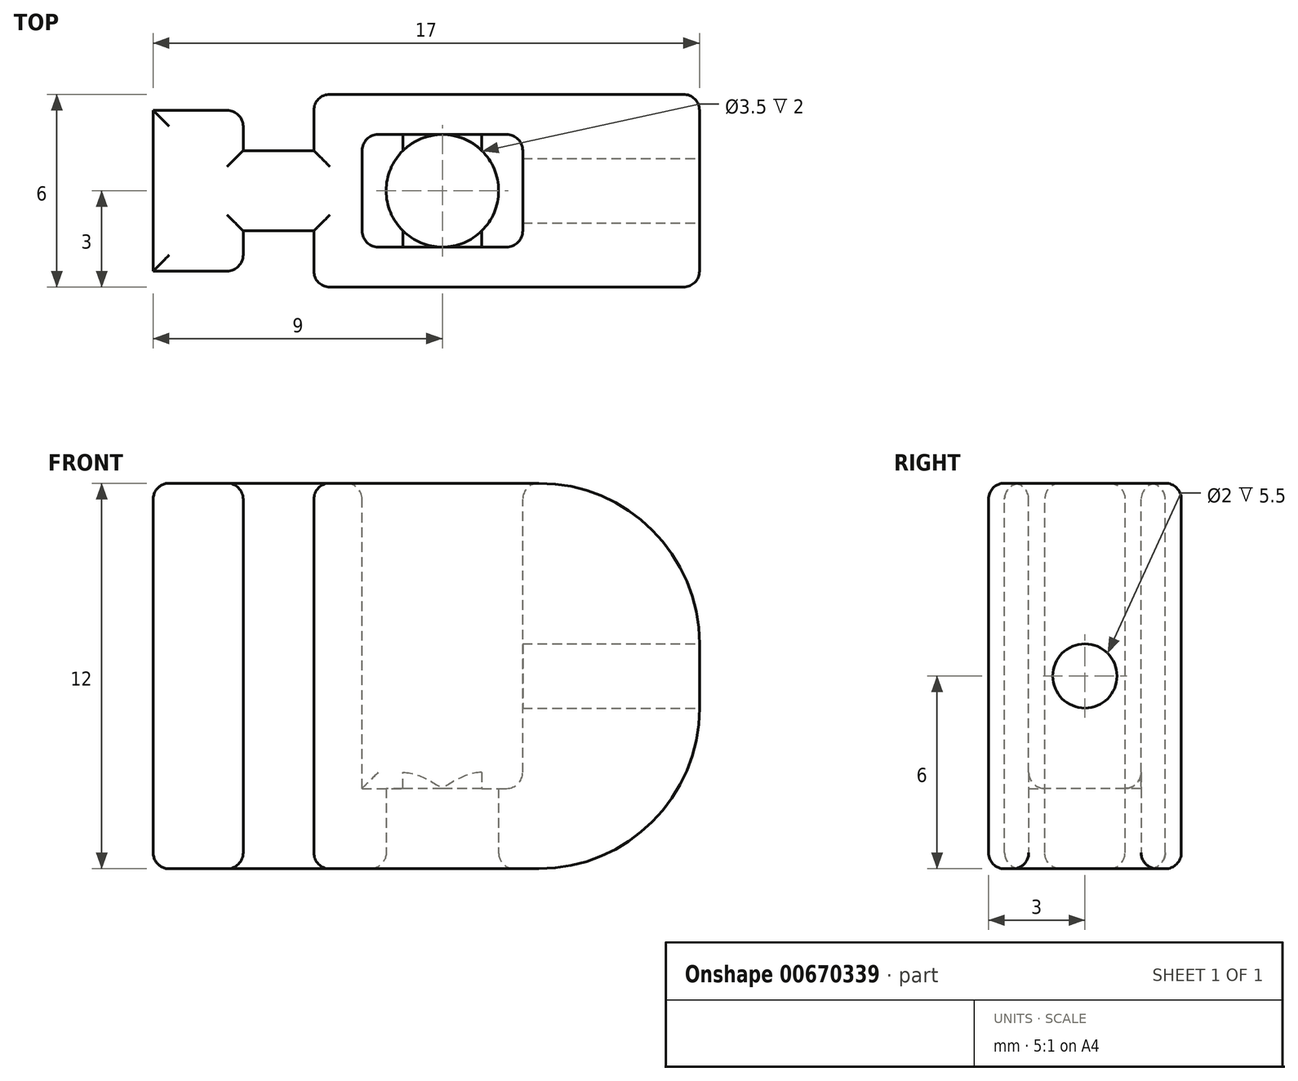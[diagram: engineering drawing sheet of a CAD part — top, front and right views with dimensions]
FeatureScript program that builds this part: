
annotation { "Feature Type Name" : "Feature", "Feature Type Description" : "" }
export const myFeature = defineFeature(function(context is Context, id is Id, definition is map)
    precondition{}
    {
        {
            var Q0;
            Q0=qCreatedBy(makeId("Top.planeOp"),FACE);
            var sketch = newSketch(context, id + "F0", { "sketchPlane" : qUnion([Q0])});
            skLineSegment(sketch, "E0.bottom", {"start": v(0, 0) * mm, "end": v(-17, 0) * mm});
            skLineSegment(sketch, "E0.top", {"start": v(0, 6) * mm, "end": v(-17, 6) * mm});
            skLineSegment(sketch, "E0.left", {"start": v(0, 0) * mm, "end": v(0, 6) * mm});
            skLineSegment(sketch, "E0.right", {"start": v(-17, 0) * mm, "end": v(-17, 6) * mm});
            skSolve(sketch);
        }
        {
            var Q0;
            Q0 = qSketchRegion(id + "F0", true);
            extrude(context, id + "F1", {"entities" : qUnion([Q0]), "depth" : 12 * mm, "offsetDistance" : 25 * mm});
        }
        {
            var Q0;
            Q0=makeQuery(id+"F1.opExtrude","CAP_FACE",FACE,{"disambiguationData":[OSD([sQuery(id+"F0.wireOp",EDGE,"E0.bottom"),sQuery(id+"F0.wireOp",EDGE,"E0.top"),sQuery(id+"F0.wireOp",EDGE,"E0.left"),sQuery(id+"F0.wireOp",EDGE,"E0.right")])],"isStart":false});
            var sketch = newSketch(context, id + "F2", { "sketchPlane" : qUnion([Q0])});
            skLineSegment(sketch, "E1", {"start": v(-17, 0) * mm, "end": v(-12, 0) * mm});
            skLineSegment(sketch, "E2", {"start": v(-12, 0) * mm, "end": v(-12, 1.75) * mm});
            skLineSegment(sketch, "E3", {"start": v(-12, 1.75) * mm, "end": v(-14.2, 1.75) * mm});
            skLineSegment(sketch, "E4", {"start": v(-14.2, 1.75) * mm, "end": v(-14.2, 0.5) * mm});
            skLineSegment(sketch, "E5", {"start": v(-14.2, 0.5) * mm, "end": v(-16.1, 0.5) * mm});
            skLineSegment(sketch, "E6", {"start": v(-16.1, 0.5) * mm, "end": v(-17, 0.5) * mm});
            skLineSegment(sketch, "E7", {"start": v(-17, 0.5) * mm, "end": v(-17, 5.5) * mm});
            skLineSegment(sketch, "E8", {"start": v(-17, 5.5) * mm, "end": v(-14.2, 5.5) * mm});
            skLineSegment(sketch, "E9", {"start": v(-14.2, 5.5) * mm, "end": v(-14.2, 4.25) * mm});
            skLineSegment(sketch, "E10", {"start": v(-14.2, 4.25) * mm, "end": v(-12, 4.25) * mm});
            skLineSegment(sketch, "E11", {"start": v(-12, 4.25) * mm, "end": v(-12, 6) * mm});
            skLineSegment(sketch, "E12", {"start": v(-12, 6) * mm, "end": v(-17.93, 6) * mm});
            skLineSegment(sketch, "E13", {"start": v(-17.93, 6) * mm, "end": v(-17.93, 0) * mm});
            skLineSegment(sketch, "E14", {"start": v(-17.93, 0) * mm, "end": v(-17, 0) * mm});
            skLineSegment(sketch, "E15", {"start": v(-21.87, 3) * mm, "end": v(11.12, 3) * mm, "construction": true});
            skSolve(sketch);
        }
        {
            var Q0;
            Q0 = qSketchRegion(id + "F2", true);
            extrude(context, id + "F3", {"entities" : qUnion([Q0]), "operationType" : NewBodyOperationType.REMOVE, "endBound" : BoundingType.THROUGH_ALL, "oppositeDirection" : true, "depth" : 25 * mm, "offsetDistance" : 25 * mm});
        }
        {
            var Q0;
            Q0=qCreatedBy(makeId("Top.planeOp"),FACE);
            var sketch = newSketch(context, id + "F4", { "sketchPlane" : qUnion([Q0])});
            skCircle(sketch, "E16", {"center": v(-8, 3) * mm, "radius": 1.75 * mm});
            skLineSegment(sketch, "E17", {"start": v(-20.02, 3) * mm, "end": v(4.02, 3) * mm, "construction": true});
            skSolve(sketch);
        }
        {
            var Q0;
            Q0 = qSketchRegion(id + "F4", true);
            extrude(context, id + "F5", {"entities" : qUnion([Q0]), "operationType" : NewBodyOperationType.REMOVE, "endBound" : BoundingType.THROUGH_ALL, "depth" : 25 * mm, "offsetDistance" : 25 * mm});
        }
        {
            var Q0;
            Q0=makeQuery(id+"F1.opExtrude","CAP_FACE",FACE,{"disambiguationData":[OSD([sQuery(id+"F0.wireOp",EDGE,"E0.bottom"),sQuery(id+"F0.wireOp",EDGE,"E0.top"),sQuery(id+"F0.wireOp",EDGE,"E0.left"),sQuery(id+"F0.wireOp",EDGE,"E0.right")])],"isStart":false});
            var sketch = newSketch(context, id + "F6", { "sketchPlane" : qUnion([Q0])});
            skLineSegment(sketch, "E18.bottom", {"start": v(-10.5, 4.75) * mm, "end": v(-5.5, 4.75) * mm});
            skLineSegment(sketch, "E18.top", {"start": v(-10.5, 1.25) * mm, "end": v(-5.5, 1.25) * mm});
            skLineSegment(sketch, "E18.left", {"start": v(-10.5, 4.75) * mm, "end": v(-10.5, 1.25) * mm});
            skLineSegment(sketch, "E18.right", {"start": v(-5.5, 4.75) * mm, "end": v(-5.5, 1.25) * mm});
            skLineSegment(sketch, "E19", {"start": v(-16.18, 3) * mm, "end": v(3.84, 3) * mm, "construction": true});
            skSolve(sketch);
        }
        {
            var Q0;
            Q0 = qSketchRegion(id + "F6", true);
            extrude(context, id + "F7", {"entities" : qUnion([Q0]), "operationType" : NewBodyOperationType.REMOVE, "oppositeDirection" : true, "depth" : 9.5 * mm, "offsetDistance" : 25 * mm});
        }
        {
            var Q0;
            Q0=makeQuery(id+"F3.boolean.opBoolean","COPY",EDGE,{"derivedFrom":makeQuery(id+"F3.opExtrude","SWEPT_EDGE",EDGE,{"disambiguationData":[OSD([sQuery(id+"F0.wireOp",EDGE,"E0.bottom"),sQuery(id+"F2.wireOp",EDGE,"E1"),sQuery(id+"F2.wireOp",EDGE,"E2")])]})});
            var Q1;
            Q1=makeQuery(id+"F3.boolean.opBoolean","COPY",EDGE,{"derivedFrom":makeQuery(id+"F3.opExtrude","SWEPT_EDGE",EDGE,{"disambiguationData":[OSD([sQuery(id+"F0.wireOp",EDGE,"E0.top"),sQuery(id+"F2.wireOp",EDGE,"E11"),sQuery(id+"F2.wireOp",EDGE,"E12")])]})});
            var Q2;
            Q2=makeQuery(id+"F3.boolean.opBoolean","COPY",EDGE,{"derivedFrom":makeQuery(id+"F3.opExtrude","SWEPT_EDGE",EDGE,{"disambiguationData":[OSD([sQuery(id+"F2.wireOp",EDGE,"E8"),sQuery(id+"F2.wireOp",EDGE,"E9")])]})});
            var Q3;
            Q3=makeQuery(id+"F3.boolean.opBoolean","COPY",EDGE,{"derivedFrom":makeQuery(id+"F3.opExtrude","SWEPT_EDGE",EDGE,{"disambiguationData":[OSD([sQuery(id+"F0.wireOp",EDGE,"E0.right"),sQuery(id+"F2.wireOp",EDGE,"E7"),sQuery(id+"F2.wireOp",EDGE,"E8")])]})});
            var Q4;
            Q4=makeQuery(id+"F3.boolean.opBoolean","COPY",EDGE,{"derivedFrom":makeQuery(id+"F3.opExtrude","SWEPT_EDGE",EDGE,{"disambiguationData":[OSD([sQuery(id+"F0.wireOp",EDGE,"E0.right"),sQuery(id+"F2.wireOp",EDGE,"E6"),sQuery(id+"F2.wireOp",EDGE,"E7")])]})});
            var Q5;
            Q5=makeQuery(id+"F3.boolean.opBoolean","COPY",EDGE,{"derivedFrom":makeQuery(id+"F3.opExtrude","SWEPT_EDGE",EDGE,{"disambiguationData":[OSD([sQuery(id+"F2.wireOp",EDGE,"E4"),sQuery(id+"F2.wireOp",EDGE,"E5")])]})});
            fillet(context, id + "F8", {"entities" : qUnion([Q0, Q1, Q2, Q3, Q4, Q5]), "radius" : 0.5 * mm, "tangentPropagation" : true, "allowEdgeOverflow" : false});
        }
        {
            var Q0;
            Q0=makeQuery(id+"F1.opExtrude","CAP_EDGE",EDGE,{"disambiguationData":[OSD([sQuery(id+"F0.wireOp",EDGE,"E0.left")])],"isStart":false});
            var Q1;
            Q1=makeQuery(id+"F1.opExtrude","CAP_EDGE",EDGE,{"disambiguationData":[OSD([sQuery(id+"F0.wireOp",EDGE,"E0.left")])],"isStart":true});
            fillet(context, id + "F9", {"entities" : qUnion([Q0, Q1]), "radius" : 5 * mm, "tangentPropagation" : true, "allowEdgeOverflow" : false});
        }
        {
            var Q0;
            Q0=makeQuery(id+"F1.opExtrude","CAP_FACE",FACE,{"disambiguationData":[OSD([sQuery(id+"F0.wireOp",EDGE,"E0.bottom"),sQuery(id+"F0.wireOp",EDGE,"E0.top"),sQuery(id+"F0.wireOp",EDGE,"E0.left"),sQuery(id+"F0.wireOp",EDGE,"E0.right")])],"isStart":true});
            var Q1;
            Q1=makeQuery(id+"F7.boolean.opBoolean","COPY",EDGE,{"derivedFrom":makeQuery(id+"F7.opExtrude","CAP_EDGE",EDGE,{"disambiguationData":[OSD([sQuery(id+"F6.wireOp",EDGE,"E18.bottom")])],"isStart":true})});
            var Q2;
            Q2=makeQuery(id+"F7.boolean.opBoolean","COPY",EDGE,{"derivedFrom":makeQuery(id+"F7.opExtrude","CAP_EDGE",EDGE,{"disambiguationData":[OSD([sQuery(id+"F6.wireOp",EDGE,"E18.left")])],"isStart":true})});
            var Q3;
            Q3=makeQuery(id+"F7.boolean.opBoolean","COPY",EDGE,{"derivedFrom":makeQuery(id+"F7.opExtrude","CAP_EDGE",EDGE,{"disambiguationData":[OSD([sQuery(id+"F6.wireOp",EDGE,"E18.top")])],"isStart":true})});
            var Q4;
            Q4=makeQuery(id+"F7.boolean.opBoolean","COPY",EDGE,{"derivedFrom":makeQuery(id+"F7.opExtrude","CAP_EDGE",EDGE,{"disambiguationData":[OSD([sQuery(id+"F6.wireOp",EDGE,"E18.right")])],"isStart":true})});
            var Q5;
            Q5=makeQuery(id+"F7.boolean.opBoolean","COPY",EDGE,{"derivedFrom":makeQuery(id+"F7.opExtrude","SWEPT_EDGE",EDGE,{"disambiguationData":[OSD([sQuery(id+"F6.wireOp",EDGE,"E18.bottom"),sQuery(id+"F6.wireOp",EDGE,"E18.right")])]})});
            var Q6;
            {var subQ0=sQuery(id+"F6.wireOp",EDGE,"E18.left");var subQ1=sQuery(id+"F6.wireOp",EDGE,"E18.top");Q6=makeQuery(id+"F7.boolean.opBoolean","COPY",EDGE,{"disambiguationData":[TD([makeQuery(id+"F7.opExtrude","SWEPT_FACE",FACE,{"disambiguationData":[OSD([subQ0])]})])],"derivedFrom":makeQuery(id+"F7.opExtrude","CAP_EDGE",EDGE,{"disambiguationData":[OSD([subQ1])],"isStart":false})});}
            var Q7;
            Q7=makeQuery(id+"F7.boolean.opBoolean","COPY",EDGE,{"derivedFrom":makeQuery(id+"F7.opExtrude","SWEPT_EDGE",EDGE,{"disambiguationData":[OSD([sQuery(id+"F6.wireOp",EDGE,"E18.top"),sQuery(id+"F6.wireOp",EDGE,"E18.left")])]})});
            fillet(context, id + "F10", {"entities" : qUnion([Q0, Q1, Q2, Q3, Q4, Q5, Q6, Q7]), "radius" : 0.5 * mm, "tangentPropagation" : true, "allowEdgeOverflow" : false});
        }
        {
            var Q0;
            Q0=makeQuery(id+"F1.opExtrude","SWEPT_FACE",FACE,{"disambiguationData":[OSD([sQuery(id+"F0.wireOp",EDGE,"E0.left")])]});
            var sketch = newSketch(context, id + "F11", { "sketchPlane" : qUnion([Q0])});
            skCircle(sketch, "E20", {"center": v(3, 6) * mm, "radius": 1 * mm});
            skPoint(sketch, "E20.centerSnap0", {"position": v(0.5, 6) * mm});
            skSolve(sketch);
        }
        {
            var Q0;
            Q0 = qSketchRegion(id + "F11", true);
            extrude(context, id + "F12", {"entities" : qUnion([Q0]), "operationType" : NewBodyOperationType.REMOVE, "endBound" : BoundingType.UP_TO_NEXT, "oppositeDirection" : true, "depth" : 25 * mm, "offsetDistance" : 25 * mm});
        }
        {
            var Q0;
            Q0=makeQuery(id+"F1.opExtrude","CAP_FACE",FACE,{"disambiguationData":[OSD([sQuery(id+"F0.wireOp",EDGE,"E0.bottom"),sQuery(id+"F0.wireOp",EDGE,"E0.top"),sQuery(id+"F0.wireOp",EDGE,"E0.left"),sQuery(id+"F0.wireOp",EDGE,"E0.right")])],"isStart":false});
            var Q1;
            Q1=makeQuery(id+"F7.boolean.opBoolean","COPY",EDGE,{"derivedFrom":makeQuery(id+"F7.opExtrude","SWEPT_EDGE",EDGE,{"disambiguationData":[OSD([sQuery(id+"F6.wireOp",EDGE,"E18.top"),sQuery(id+"F6.wireOp",EDGE,"E18.right")])]})});
            var Q2;
            Q2=makeQuery(id+"F7.boolean.opBoolean","COPY",EDGE,{"derivedFrom":makeQuery(id+"F7.opExtrude","SWEPT_EDGE",EDGE,{"disambiguationData":[OSD([sQuery(id+"F6.wireOp",EDGE,"E18.bottom"),sQuery(id+"F6.wireOp",EDGE,"E18.left")])]})});
            fillet(context, id + "F13", {"entities" : qUnion([Q0, Q1, Q2]), "radius" : 0.5 * mm, "tangentPropagation" : true, "allowEdgeOverflow" : false});
        }
    });
